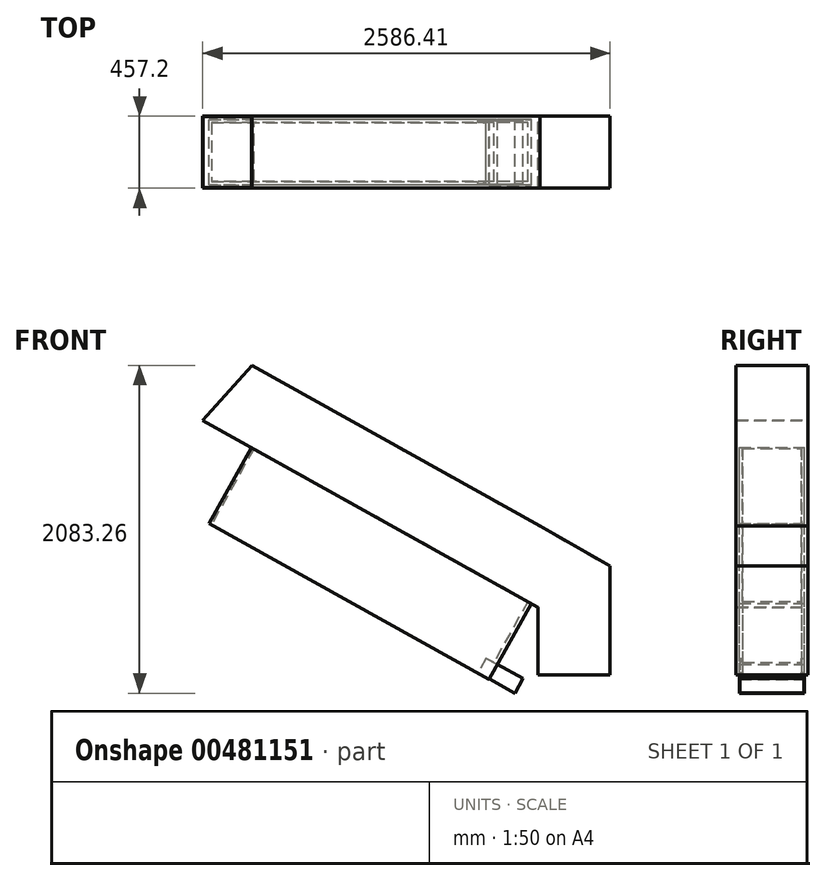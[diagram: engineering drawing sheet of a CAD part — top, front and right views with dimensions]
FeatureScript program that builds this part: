
annotation { "Feature Type Name" : "Feature", "Feature Type Description" : "" }
export const myFeature = defineFeature(function(context is Context, id is Id, definition is map)
    precondition{}
    {
        {
            var Q0;
            Q0=qCreatedBy(makeId("Front.planeOp"),FACE);
            var sketch = newSketch(context, id + "F0", { "sketchPlane" : qUnion([Q0])});
            skLineSegment(sketch, "E0", {"start": v(135.78, 917.9) * mm, "end": v(1964.58, -102.81) * mm});
            skLineSegment(sketch, "E1", {"start": v(-176.95, 568.85) * mm, "end": v(1952.26, -619.52) * mm});
            skLineSegment(sketch, "E2", {"start": v(1964.58, -102.81) * mm, "end": v(2409.46, -357.95) * mm});
            skLineSegment(sketch, "E3", {"start": v(2409.46, -357.95) * mm, "end": v(2409.46, -1047.1) * mm});
            skLineSegment(sketch, "E4", {"start": v(1952.26, -619.52) * mm, "end": v(1952.26, -1047.1) * mm});
            skLineSegment(sketch, "E5", {"start": v(135.78, 917.9) * mm, "end": v(-176.95, 568.85) * mm});
            skLineSegment(sketch, "E6", {"start": v(2409.46, -1047.1) * mm, "end": v(1952.26, -1047.1) * mm});
            skSolve(sketch);
        }
        {
            var Q0;
            Q0=makeQuery(id+"F0.imprint","IMPRINT",FACE,{"disambiguationData":[TD([[makeQuery(id+"F0.imprint","IMPRINT",EDGE,{"derivedFrom":sQuery(id+"F0.wireOp",EDGE,"E0")}),-1.0]])]});
            extrude(context, id + "F1", {"entities" : qUnion([Q0]), "endBound" : BoundingType.SYMMETRIC, "depth" : 457.2 * mm});
        }
        {
            var Q0;
            Q0=makeQuery(id+"F1.opExtrude","SWEPT_FACE",FACE,{"disambiguationData":[OSD([sQuery(id+"F0.wireOp",EDGE,"E6")])]});
            var Q1;
            Q1=makeQuery(id+"F1.opExtrude","SWEPT_FACE",FACE,{"disambiguationData":[OSD([sQuery(id+"F0.wireOp",EDGE,"E5")])]});
            shell(context, id + "F2", {"entities" : qUnion([Q0, Q1]), "thickness" : 3.17 * mm});
        }
        {
            var Q0;
            Q0=makeQuery(id+"F1.opExtrude","SWEPT_FACE",FACE,{"disambiguationData":[OSD([sQuery(id+"F0.wireOp",EDGE,"E1")])]});
            var sketch = newSketch(context, id + "F3", { "sketchPlane" : qUnion([Q0])});
            skLineSegment(sketch, "E7.bottom", {"start": v(1958.39, 207.21) * mm, "end": v(-77.5, 207.21) * mm});
            skLineSegment(sketch, "E7.top", {"start": v(1958.39, -207.8) * mm, "end": v(-77.5, -207.8) * mm});
            skLineSegment(sketch, "E7.left", {"start": v(1958.39, 207.21) * mm, "end": v(1958.39, -207.8) * mm});
            skLineSegment(sketch, "E7.right", {"start": v(-77.5, 207.21) * mm, "end": v(-77.5, -207.8) * mm});
            skSolve(sketch);
        }
        {
            var Q0;
            Q0 = qSketchRegion(id + "F3", true);
            extrude(context, id + "F4", {"entities" : qUnion([Q0]), "operationType" : NewBodyOperationType.ADD, "depth" : 551.18 * mm});
        }
        {
            var Q0;
            Q0=makeQuery(id+"F4.opExtrude","CAP_FACE",FACE,{"disambiguationData":[OSD([sQuery(id+"F3.wireOp",EDGE,"E7.bottom"),sQuery(id+"F3.wireOp",EDGE,"E7.top"),sQuery(id+"F3.wireOp",EDGE,"E7.left"),sQuery(id+"F3.wireOp",EDGE,"E7.right")])],"isStart":false});
            var sketch = newSketch(context, id + "F5", { "sketchPlane" : qUnion([Q0])});
            skLineSegment(sketch, "E8.bottom", {"start": v(-60.36, -187.38) * mm, "end": v(1932.53, -187.38) * mm});
            skLineSegment(sketch, "E8.top", {"start": v(-60.36, 186.54) * mm, "end": v(1932.53, 186.54) * mm});
            skLineSegment(sketch, "E8.left", {"start": v(-60.36, -187.38) * mm, "end": v(-60.36, 186.54) * mm});
            skLineSegment(sketch, "E8.right", {"start": v(1932.53, -187.38) * mm, "end": v(1932.53, 186.54) * mm});
            skSolve(sketch);
        }
        {
            var Q0;
            Q0=makeQuery(id+"F5.imprint","IMPRINT",FACE,{"disambiguationData":[TD([[makeQuery(id+"F5.imprint","IMPRINT",EDGE,{"derivedFrom":sQuery(id+"F5.wireOp",EDGE,"E8.bottom")}),1.0]])]});
            extrude(context, id + "F6", {"entities" : qUnion([Q0]), "operationType" : NewBodyOperationType.REMOVE, "oppositeDirection" : true, "depth" : 759.46 * mm});
        }
        {
            var Q0;
            Q0=makeQuery(id+"F4.opExtrude","SWEPT_FACE",FACE,{"disambiguationData":[OSD([sQuery(id+"F3.wireOp",EDGE,"E7.left")])]});
            var sketch = newSketch(context, id + "F7", { "sketchPlane" : qUnion([Q0])});
            skLineSegment(sketch, "E9.bottom", {"start": v(-204.93, -138.08) * mm, "end": v(206.08, -138.08) * mm});
            skLineSegment(sketch, "E9.top", {"start": v(-204.93, -30.78) * mm, "end": v(206.08, -30.78) * mm});
            skLineSegment(sketch, "E9.left", {"start": v(-204.93, -138.08) * mm, "end": v(-204.93, -30.78) * mm});
            skLineSegment(sketch, "E9.right", {"start": v(206.08, -138.08) * mm, "end": v(206.08, -30.78) * mm});
            skSolve(sketch);
        }
        {
            var Q0;
            Q0 = qSketchRegion(id + "F7", true);
            extrude(context, id + "F8", {"entities" : qUnion([Q0]), "operationType" : NewBodyOperationType.ADD, "depth" : 185.42 * mm});
        }
        {
            var Q0;
            Q0=makeQuery(id+"F8.opExtrude","CAP_FACE",FACE,{"disambiguationData":[OSD([sQuery(id+"F7.wireOp",EDGE,"E9.bottom"),sQuery(id+"F7.wireOp",EDGE,"E9.top"),sQuery(id+"F7.wireOp",EDGE,"E9.left"),sQuery(id+"F7.wireOp",EDGE,"E9.right")])],"isStart":false});
            var sketch = newSketch(context, id + "F9", { "sketchPlane" : qUnion([Q0])});
            skLineSegment(sketch, "E10.bottom", {"start": v(-202.21, -31.63) * mm, "end": v(202.2, -31.63) * mm});
            skLineSegment(sketch, "E10.top", {"start": v(-202.21, -136.85) * mm, "end": v(202.2, -136.85) * mm});
            skLineSegment(sketch, "E10.left", {"start": v(-202.21, -31.63) * mm, "end": v(-202.21, -136.85) * mm});
            skLineSegment(sketch, "E10.right", {"start": v(202.2, -31.63) * mm, "end": v(202.2, -136.85) * mm});
            skSolve(sketch);
        }
        {
            var Q0;
            Q0=makeQuery(id+"F9.imprint","IMPRINT",FACE,{"disambiguationData":[TD([[makeQuery(id+"F9.imprint","IMPRINT",EDGE,{"derivedFrom":sQuery(id+"F9.wireOp",EDGE,"E10.bottom")}),-1.0]])]});
            extrude(context, id + "F10", {"entities" : qUnion([Q0]), "operationType" : NewBodyOperationType.REMOVE, "oppositeDirection" : true, "depth" : 266.95 * mm});
        }
    });
